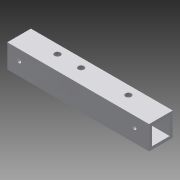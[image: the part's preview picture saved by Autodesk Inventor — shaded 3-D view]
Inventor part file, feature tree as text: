
AUTODESK INVENTOR PART (.ipt)
format: ipt  version: 2015 SP1 (Build 190203100, 203)  size: 127,488 bytes
history: native  units: in
note: dims shown in document units (in); Inventor stores cm internally (conversion verified against a paired STEP export)
features: sketch x4, hole x3, extrude x1
ambient origin geometry x8: Origin, YZ Plane, XZ Plane, XY Plane, X Axis, Y Axis, Z Axis, Center Point
bodies: Solid1 (feature_tree)
feature tree (8):
  extrude  "Extrusion1"  Depth=1.0in
  hole  "Hole1"  [1 undecoded]
  hole  "Hole2"  [1 undecoded]
  hole  "Hole3"  [1 undecoded]
  sketch  "Sketch1"  dims[d0=1.0in d1=1.0in]
  sketch  "Sketch2"  dims[d2=0.75in d3=0.75in]
  sketch  "Sketch3"  dims[d4=0.125in d5=0.125in]
  sketch  "Sketch4"  dims[d6=6.0in d7=0.0in d8=1.5in d9=0.625in d10=0.625in d11=1.5in d12=0.25in d13=0.75in d14=0.375in d15=0.25in d16=0.5635in d17=1.0in d18=0.8108in d19=0.625in d20=0.5625in d21=0.5in d22=0.5625in d23=0.1719in d24=0.75in d25=0.375in d26=0.25in d27=0.5635in d28=1.0in d29=0.8108in d30=0.625in d32=0.25in d33=0.75in d34=0.375in d35=0.25in d36=0.5635in d37=1.0in d38=0.8108in d39=2.5in]
note: 3 required parameter values undecoded (feature->parameter linkage not recoverable at this tier; creation-order binding heuristic only, values carry confidence <= 0.55)
